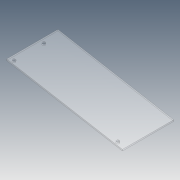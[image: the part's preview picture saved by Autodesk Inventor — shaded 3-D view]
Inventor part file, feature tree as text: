
AUTODESK INVENTOR PART (.ipt)
format: ipt  version: 2012 (Build 160160000, 160)  size: 78,336 bytes
history: native  units: in
note: dims shown in document units (in); Inventor stores cm internally (conversion verified against a paired STEP export)
features: pattern_linear x2, extrude x1, hole x1, sketch x1, reference x1
ambient origin geometry x8: Origin, YZ Plane, XZ Plane, XY Plane, X Axis, Y Axis, Z Axis, Center Point
bodies: Solid1 (feature_tree)
feature tree (6):
  extrude  "Extrusion1"  Depth=0.375in
  hole  "Hole1"  [1 undecoded]
  pattern_linear  "Rectangular Pattern1"  Count1=2 Spacing1=9.5in
  pattern_linear  "Rectangular Pattern2"  [2 undecoded]
  sketch  "Sketch1"  dims[d0=4.625in d1=0.0in d2=0.375in d3=0.3125in d4=0.265in d5=0.75in d6=0.375in d7=0.25in d8=0.5635in d9=1.0in d10=0.8108in d11=0.7874in d13=2.6875in d14=0.7874in d16=9.5in]
  reference  "Reference1"
note: 3 required parameter values undecoded (feature->parameter linkage not recoverable at this tier; creation-order binding heuristic only, values carry confidence <= 0.55)
